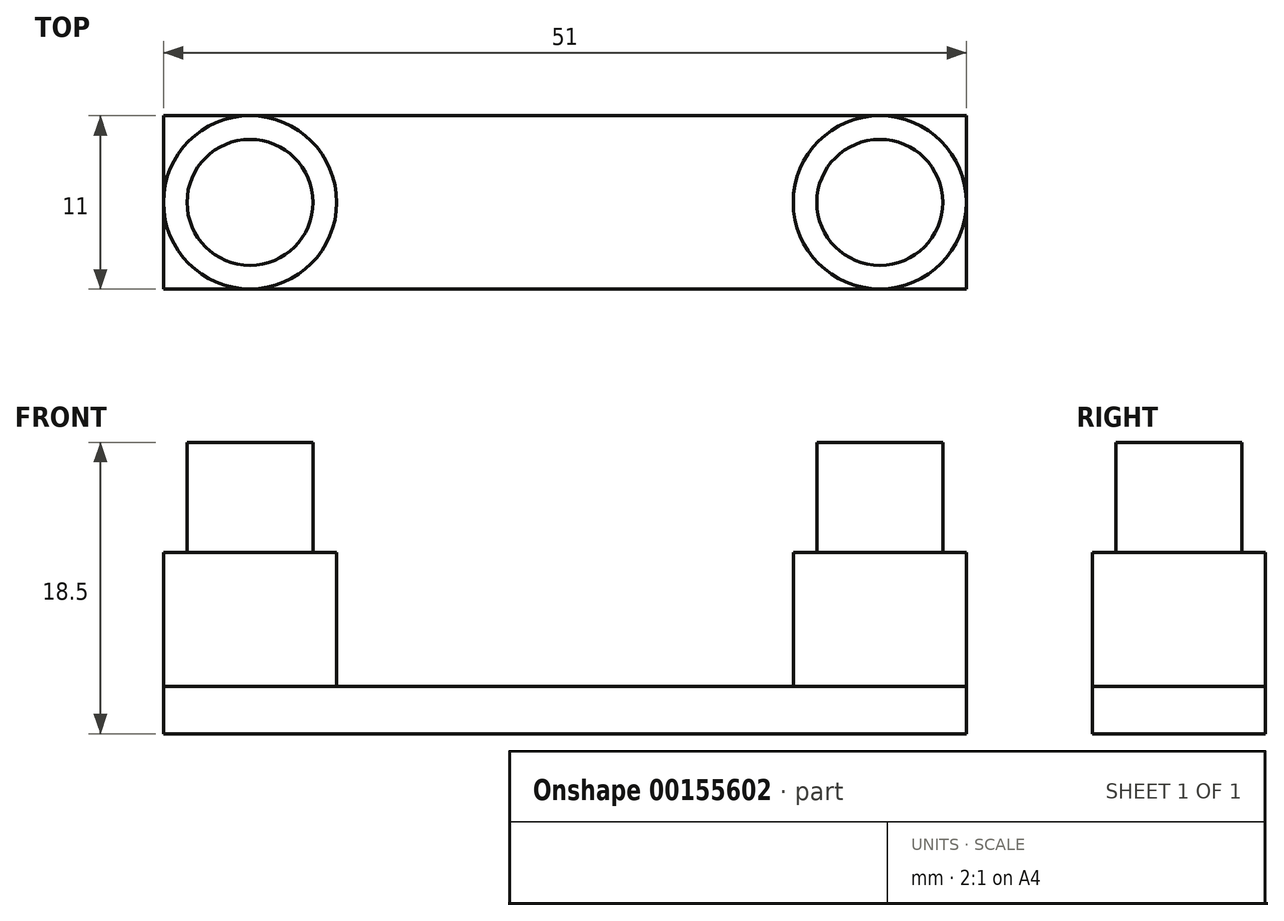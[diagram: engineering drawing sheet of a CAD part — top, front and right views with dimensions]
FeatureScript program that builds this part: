
annotation { "Feature Type Name" : "Feature", "Feature Type Description" : "" }
export const myFeature = defineFeature(function(context is Context, id is Id, definition is map)
    precondition{}
    {
        {
            var Q0;
            Q0=qCreatedBy(makeId("Top.planeOp"),FACE);
            var sketch = newSketch(context, id + "F0", { "sketchPlane" : qUnion([Q0])});
            skLineSegment(sketch, "E0.bottom", {"start": v(0, 0) * mm, "end": v(51, 0) * mm});
            skLineSegment(sketch, "E0.top", {"start": v(0, 11) * mm, "end": v(51, 11) * mm});
            skLineSegment(sketch, "E0.left", {"start": v(0, 0) * mm, "end": v(0, 11) * mm});
            skLineSegment(sketch, "E0.right", {"start": v(51, 0) * mm, "end": v(51, 11) * mm});
            skLineSegment(sketch, "E1", {"start": v(0, 5.5) * mm, "end": v(51, 5.5) * mm});
            skCircle(sketch, "E2", {"center": v(5.5, 5.5) * mm, "radius": 5.5 * mm});
            skCircle(sketch, "E3", {"center": v(45.5, 5.5) * mm, "radius": 5.5 * mm});
            skCircle(sketch, "E4", {"center": v(5.5, 5.5) * mm, "radius": 4 * mm});
            skCircle(sketch, "E5", {"center": v(45.5, 5.5) * mm, "radius": 4 * mm});
            skCircle(sketch, "E6", {"center": v(5.5, 5.5) * mm, "radius": 11 * mm, "construction": true});
            skCircle(sketch, "E7", {"center": v(45.5, 5.5) * mm, "radius": 11 * mm, "construction": true});
            skSolve(sketch);
        }
        {
            var Q0;
            Q0 = qSketchRegion(id + "F0", true);
            extrude(context, id + "F1", {"entities" : qUnion([Q0]), "depth" : 3 * mm});
        }
        {
            var Q0;
            {var subQ2=sQuery(id+"F0.wireOp",EDGE,"E1");var subQ5=sQuery(id+"F0.wireOp",EDGE,"E4");var subQ6=makeQuery(id+"F0.imprint","INTERSECT",VERTEX,{"disambiguationData":[OD(1.0)],"derivedFrom":[subQ2,subQ5]});Q0=makeQuery(id+"F0.imprint","IMPRINT",FACE,{"disambiguationData":[TD([[makeQuery(id+"F0.imprint","IMPRINT",EDGE,{"disambiguationData":[TD([[subQ6,-1.0]])],"derivedFrom":subQ2}),-1.0]])]});}
            var Q1;
            {var subQ1=sQuery(id+"F0.wireOp",EDGE,"E1");var subQ4=sQuery(id+"F0.wireOp",EDGE,"E4");var subQ6=makeQuery(id+"F0.imprint","INTERSECT",VERTEX,{"disambiguationData":[OD(1.0)],"derivedFrom":[subQ1,subQ4]});Q1=makeQuery(id+"F0.imprint","IMPRINT",FACE,{"disambiguationData":[TD([[makeQuery(id+"F0.imprint","IMPRINT",EDGE,{"disambiguationData":[TD([[subQ6,-1.0]])],"derivedFrom":subQ1}),1.0]])]});}
            var Q2;
            {var subQ0=sQuery(id+"F0.wireOp",EDGE,"E3");var subQ2=sQuery(id+"F0.wireOp",EDGE,"E1");var subQ3=makeQuery(id+"F0.imprint","INTERSECT",VERTEX,{"derivedFrom":[subQ2,subQ0]});Q2=makeQuery(id+"F0.imprint","IMPRINT",FACE,{"disambiguationData":[TD([[makeQuery(id+"F0.imprint","IMPRINT",EDGE,{"disambiguationData":[TD([[subQ3,-1.0]])],"derivedFrom":subQ2}),1.0]])]});}
            var Q3;
            {var subQ0=sQuery(id+"F0.wireOp",EDGE,"E3");var subQ1=sQuery(id+"F0.wireOp",EDGE,"E1");var subQ4=makeQuery(id+"F0.imprint","INTERSECT",VERTEX,{"derivedFrom":[subQ1,subQ0]});Q3=makeQuery(id+"F0.imprint","IMPRINT",FACE,{"disambiguationData":[TD([[makeQuery(id+"F0.imprint","IMPRINT",EDGE,{"disambiguationData":[TD([[subQ4,-1.0]])],"derivedFrom":subQ1}),-1.0]])]});}
            extrude(context, id + "F2", {"entities" : qUnion([Q0, Q1, Q2, Q3]), "operationType" : NewBodyOperationType.ADD, "depth" : 11.5 * mm});
        }
        {
            var Q0;
            {var subQ0=sQuery(id+"F0.wireOp",EDGE,"E5");var subQ1=sQuery(id+"F0.wireOp",EDGE,"E1");var subQ2=makeQuery(id+"F0.imprint","INTERSECT",VERTEX,{"disambiguationData":[OD(0.0)],"derivedFrom":[subQ1,subQ0]});Q0=makeQuery(id+"F0.imprint","IMPRINT",FACE,{"disambiguationData":[TD([[makeQuery(id+"F0.imprint","IMPRINT",EDGE,{"disambiguationData":[TD([[subQ2,-1.0]])],"derivedFrom":subQ1}),1.0]])]});}
            var Q1;
            {var subQ0=sQuery(id+"F0.wireOp",EDGE,"E5");var subQ1=sQuery(id+"F0.wireOp",EDGE,"E1");var subQ2=makeQuery(id+"F0.imprint","INTERSECT",VERTEX,{"disambiguationData":[OD(0.0)],"derivedFrom":[subQ1,subQ0]});Q1=makeQuery(id+"F0.imprint","IMPRINT",FACE,{"disambiguationData":[TD([[makeQuery(id+"F0.imprint","IMPRINT",EDGE,{"disambiguationData":[TD([[subQ2,-1.0]])],"derivedFrom":subQ1}),-1.0]])]});}
            var Q2;
            {var subQ0=sQuery(id+"F0.wireOp",EDGE,"E4");var subQ1=sQuery(id+"F0.wireOp",EDGE,"E1");var subQ2=makeQuery(id+"F0.imprint","INTERSECT",VERTEX,{"disambiguationData":[OD(0.0)],"derivedFrom":[subQ1,subQ0]});Q2=makeQuery(id+"F0.imprint","IMPRINT",FACE,{"disambiguationData":[TD([[makeQuery(id+"F0.imprint","IMPRINT",EDGE,{"disambiguationData":[TD([[subQ2,-1.0]])],"derivedFrom":subQ1}),1.0]])]});}
            var Q3;
            {var subQ0=sQuery(id+"F0.wireOp",EDGE,"E4");var subQ1=sQuery(id+"F0.wireOp",EDGE,"E1");var subQ2=makeQuery(id+"F0.imprint","INTERSECT",VERTEX,{"disambiguationData":[OD(0.0)],"derivedFrom":[subQ1,subQ0]});Q3=makeQuery(id+"F0.imprint","IMPRINT",FACE,{"disambiguationData":[TD([[makeQuery(id+"F0.imprint","IMPRINT",EDGE,{"disambiguationData":[TD([[subQ2,-1.0]])],"derivedFrom":subQ1}),-1.0]])]});}
            extrude(context, id + "F3", {"entities" : qUnion([Q0, Q1, Q2, Q3]), "operationType" : NewBodyOperationType.ADD, "depth" : (11.5 + 7) * mm});
        }
    });
